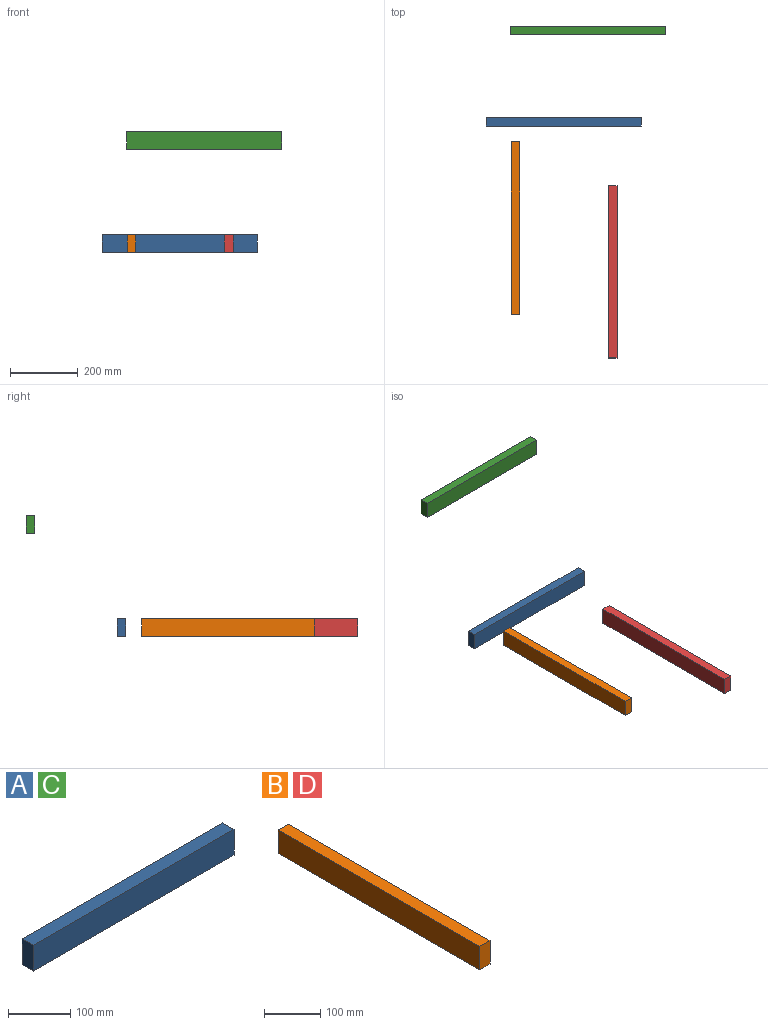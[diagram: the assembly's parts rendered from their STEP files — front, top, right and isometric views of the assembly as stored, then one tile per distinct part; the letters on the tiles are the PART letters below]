
ASSEMBLY  parts=4 mates=6
PART A: 6 faces, bbox 457.2x25.4x50.8 mm
  f0: plane 50.8x25.4mm, normal (-1,0,0), area 1290.3mm2, adj f1,f3,f4,f5
  f1: plane 457.2x50.8mm, normal (0,-1,0), area 23225.8mm2, adj f0,f2,f4,f5
  f2: plane 50.8x25.4mm, normal (1,0,0), area 1290.3mm2, adj f1,f3,f4,f5
  f3: plane 457.2x50.8mm, normal (0,1,0), area 23225.8mm2, adj f0,f2,f4,f5
  f4: plane 457.2x25.4mm, normal (0,0,1), area 11612.9mm2, adj f0,f1,f2,f3
  f5: plane 457.2x25.4mm, normal (0,0,-1), area 11612.9mm2, adj f0,f1,f2,f3
PART B: 6 faces, bbox 25.4x508x50.8 mm
  f0: plane 50.8x25.4mm, normal (0,1,0), area 1290.3mm2, adj f1,f3,f4,f5
  f1: plane 508x50.8mm, normal (-1,0,0), area 25806.4mm2, adj f0,f2,f4,f5
  f2: plane 50.8x25.4mm, normal (0,-1,0), area 1290.3mm2, adj f1,f3,f4,f5
  f3: plane 508x50.8mm, normal (1,0,0), area 25806.4mm2, adj f0,f2,f4,f5
  f4: plane 508x25.4mm, normal (0,0,1), area 12903.2mm2, adj f0,f1,f2,f3
  f5: plane 508x25.4mm, normal (0,0,-1), area 12903.2mm2, adj f0,f1,f2,f3
PART C: same geometry as A
PART D: same geometry as B
PLACE A t=(-139.95,-123.77,-231.14)mm
PLACE B t=(-142.48,-46.68,-231.14)mm
PLACE C t=(-68.46,144.98,72.43)mm
PLACE D t=(144.01,-175.3,-231.14)mm
MATE planar B.f4 <-> A.f4  axis (0,0,1) through (-53.83,-424.45,-180.34)mm
MATE parallel D.f0 <-> A.f1  axis (0,1,0) through (232.66,-299.07,-205.74)mm
MATE parallel A.f1 <-> B.f0  axis (0,-1,0) through (88.65,-123.77,-205.74)mm
MATE planar D.f4 <-> A.f4  axis (0,0,1) through (232.66,-553.07,-180.34)mm
MATE parallel D.f3 <-> A.f2  axis (1,0,0) through (245.36,-553.07,-231.14)mm
MATE parallel B.f1 <-> A.f0  axis (-1,0,0) through (-66.53,-424.45,-205.74)mm
